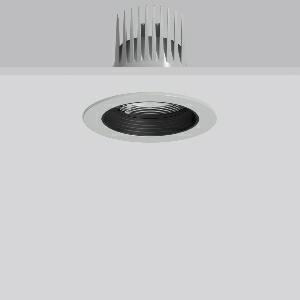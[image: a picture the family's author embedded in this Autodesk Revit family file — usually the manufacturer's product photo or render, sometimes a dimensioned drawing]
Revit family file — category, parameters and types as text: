
# Revit family: heledon_maxi_e_901768_004_3_97f6
name_source: partatom
category: Lighting Fixtures
units: mm (PartAtom-declared; Revit-internal decimal feet)

## family parameters
Cut with Voids When Loaded = No
Host = Face
Light Source = No
Part Type = Normal
Room Calculation Point = No
Round Connector Dimension = Use Diameter
Shared = No

## types (1)
- HELEDON maxi E (1 x LED Modul 935, 3600 lm, 3500)
    Apparent Load = 35 VA
    Approval mark = CE
    CIE Flux Codes = 96 100 100 100 100
    Color Rendering = 92
    Color Temperature = 3500
    Default Elevation = 1800 mm
    Description = Series: HELEDON maxi
Round recessed downlight. Housing: die-cast aluminium, powder-coated. Black plastic ring and recessed LED to prevent glare from the side. Optical assembly with lens made of plastic (polycarbonate) for the best homogeneous light distribution - can be changed without tools. Best colour rendering index Ra>90. Suitable for Recessed ceiling mounting. Installation without tools thanks to spring fastening system. Including separate LED converter with connecting cable 600 mm.High quality converter without flickering and stroboscopic effect. Through-wiring box (5 pole) available as accessory. The following accessories can be mounted without use of tools: interchangeable lenses, decorative glasses, honeycomb louvre, clear and frosted diffusers, white interchangeable plastic ring. 
Colour: silver
Diameter: 162 mm
Height: 3 mm
Cut-out diameter: 152 mm
Recess height: 200 mm
Luminaire: recess height: 135 mm
Lamp: LED
Socket: without socket
Colour temperature: 3500K
Colour rendering index (CRI): 92
System power: 35 W
Rated luminous flux: 3600 lm
Luminous efficiency: 103 lm/W
Control gear: Regulated power supply
Protection class: II
Type of protection: IP 20
    Height = 0 mm  [stored 0 ft]
    Lamp = 1 x LED Modul 935
    Lamp Light Flux = 3600 lm
    Lamp count = 1
    Length = 162 mm
    Lifetime = 50000 h
    Luminous efficacy = 103 lm/W
    Manufacturer = RZB
    ModVariant = No
    Model = 901768.004.3
    Mounting Place = Ceiling
    Mounting Type = Recessed
    Number of Poles = 1
    OnlyDefault = Yes
    Power Factor = 1
    Product Name = HELEDON maxi E
    Product group = Recessed downlights
    ProductGroupID = 402
    Protection Class = Protection class II
    Protection Degree = IP 20
    RLX_Detail_Level = 1
    RLX_Emergency_Light_Flux = 0 lm
    RLX_Emergency_Type = 0
    RLX_Emergency_Type_DB = No
    RlxData = <blob elided: 119393 chars, md5=f3b3710f>
    Socket = socket
    Standby Power = 0 W
    System Light Flux = 3600 lm
    System Power = 35 W
    Type Comments = Product without accessories
    Type Image = 901663.004.jpg
    URL = http://relux.com
    VarID = ---
    Voltage = 230 V
    Voltage Range = 220-240 V
    Weight = 0.00 kg
    Width = 0 mm  [stored 0 ft]

note: [stored X ft] marks values corroborated as IEEE doubles in the binary element streams (Revit-internal decimal feet)

## geometry (parser evidence)
native form markers: Blend x4, Sweep x11
no freeform markers — native parametric forms only
